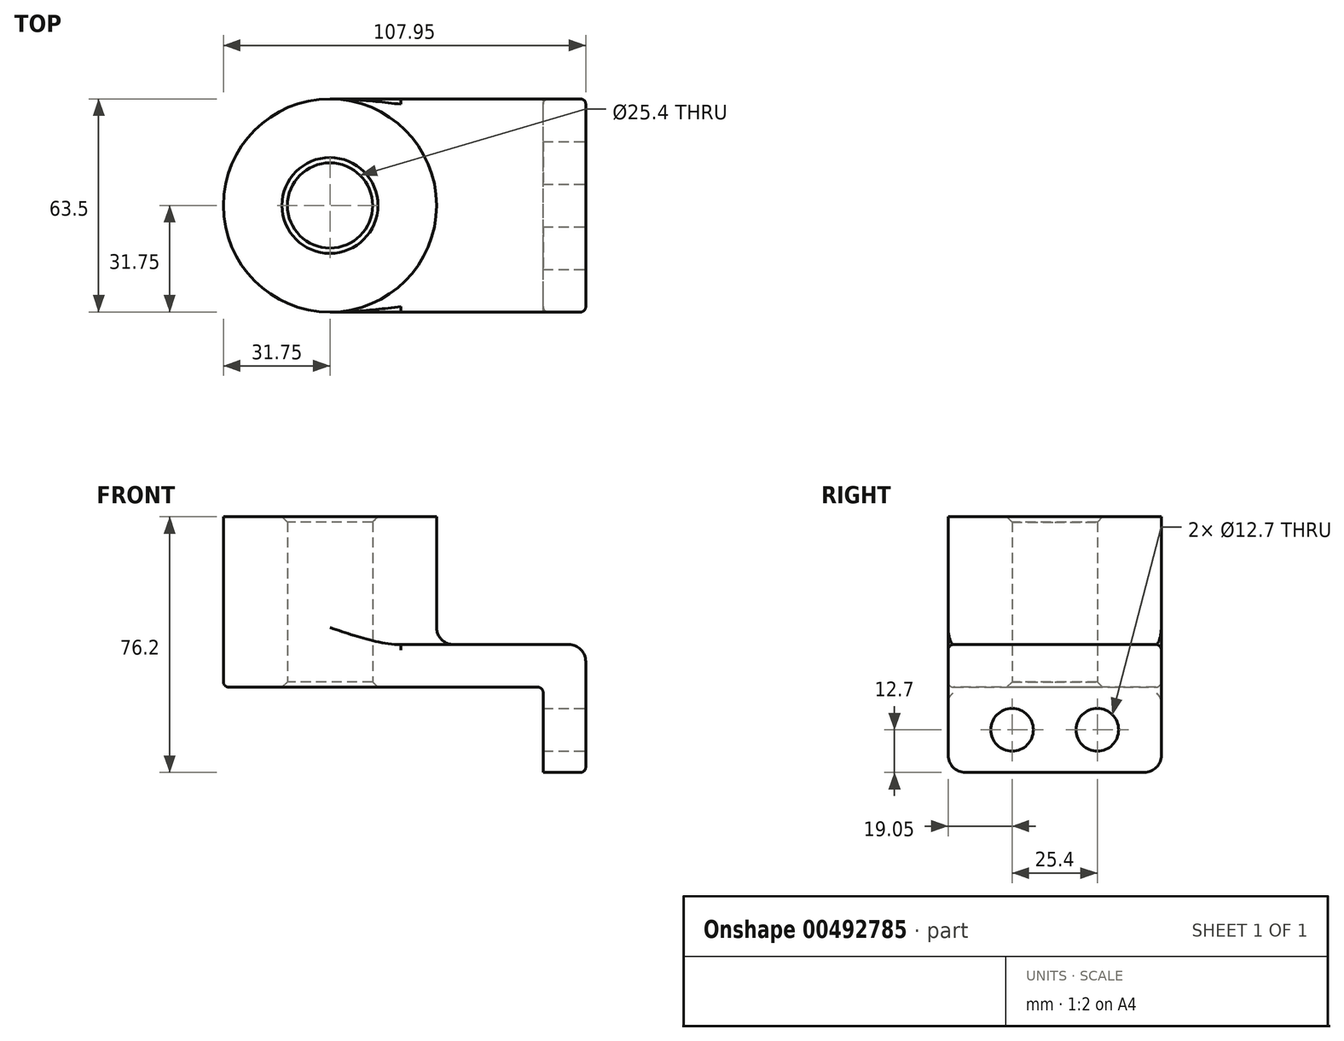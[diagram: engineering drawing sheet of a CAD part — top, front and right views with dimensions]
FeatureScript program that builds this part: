
annotation { "Feature Type Name" : "Feature", "Feature Type Description" : "" }
export const myFeature = defineFeature(function(context is Context, id is Id, definition is map)
    precondition{}
    {
        {
            var Q0;
            Q0=qCreatedBy(makeId("Top.planeOp"),FACE);
            var sketch = newSketch(context, id + "F0", { "sketchPlane" : qUnion([Q0])});
            skLineSegment(sketch, "E0.bottom", {"start": v(-38.1, -31.75) * mm, "end": v(38.1, -31.75) * mm});
            skLineSegment(sketch, "E0.top", {"start": v(-38.1, 31.75) * mm, "end": v(38.1, 31.75) * mm});
            skLineSegment(sketch, "E0.left", {"start": v(-38.1, -31.75) * mm, "end": v(-38.1, 31.75) * mm});
            skLineSegment(sketch, "E0.right", {"start": v(38.1, -31.75) * mm, "end": v(38.1, 31.75) * mm});
            skPoint(sketch, "E0.middle", {"position": v(0, 0) * mm});
            skCircle(sketch, "E1", {"center": v(-38.1, 0) * mm, "radius": 31.75 * mm});
            skCircle(sketch, "E2", {"center": v(-38.1, 0) * mm, "radius": 12.7 * mm});
            skSolve(sketch);
        }
        {
            var Q0;
            {var subQ0=sQuery(id+"F0.wireOp",EDGE,"E0.bottom");Q0=makeQuery(id+"F0.imprint","IMPRINT",FACE,{"disambiguationData":[TD([[makeQuery(id+"F0.imprint","IMPRINT",EDGE,{"derivedFrom":subQ0}),1.0]])]});}
            var Q1;
            {var subQ1=sQuery(id+"F0.wireOp",EDGE,"E0.left");var subQ3=sQuery(id+"F0.wireOp",EDGE,"E2");var subQ4=makeQuery(id+"F0.imprint","INTERSECT",VERTEX,{"disambiguationData":[OD(0.0)],"derivedFrom":[subQ1,subQ3]});Q1=makeQuery(id+"F0.imprint","IMPRINT",FACE,{"disambiguationData":[TD([[makeQuery(id+"F0.imprint","IMPRINT",EDGE,{"disambiguationData":[TD([[subQ4,-1.0]])],"derivedFrom":subQ3}),-1.0]])]});}
            var Q2;
            {var subQ1=sQuery(id+"F0.wireOp",EDGE,"E0.left");var subQ3=sQuery(id+"F0.wireOp",EDGE,"E2");var subQ4=makeQuery(id+"F0.imprint","INTERSECT",VERTEX,{"disambiguationData":[OD(0.0)],"derivedFrom":[subQ1,subQ3]});Q2=makeQuery(id+"F0.imprint","IMPRINT",FACE,{"disambiguationData":[TD([[makeQuery(id+"F0.imprint","IMPRINT",EDGE,{"disambiguationData":[TD([[subQ4,1.0]])],"derivedFrom":subQ3}),-1.0]])]});}
            extrude(context, id + "F1", {"entities" : qUnion([Q0, Q1, Q2]), "depth" : 12.7 * mm});
        }
        {
            var Q0;
            {var subQ1=sQuery(id+"F0.wireOp",EDGE,"E0.left");var subQ3=sQuery(id+"F0.wireOp",EDGE,"E2");var subQ4=makeQuery(id+"F0.imprint","INTERSECT",VERTEX,{"disambiguationData":[OD(0.0)],"derivedFrom":[subQ1,subQ3]});Q0=makeQuery(id+"F0.imprint","IMPRINT",FACE,{"disambiguationData":[TD([[makeQuery(id+"F0.imprint","IMPRINT",EDGE,{"disambiguationData":[TD([[subQ4,-1.0]])],"derivedFrom":subQ3}),-1.0]])]});}
            var Q1;
            {var subQ1=sQuery(id+"F0.wireOp",EDGE,"E0.left");var subQ3=sQuery(id+"F0.wireOp",EDGE,"E2");var subQ4=makeQuery(id+"F0.imprint","INTERSECT",VERTEX,{"disambiguationData":[OD(0.0)],"derivedFrom":[subQ1,subQ3]});Q1=makeQuery(id+"F0.imprint","IMPRINT",FACE,{"disambiguationData":[TD([[makeQuery(id+"F0.imprint","IMPRINT",EDGE,{"disambiguationData":[TD([[subQ4,1.0]])],"derivedFrom":subQ3}),-1.0]])]});}
            extrude(context, id + "F2", {"entities" : qUnion([Q0, Q1]), "operationType" : NewBodyOperationType.ADD, "depth" : 50.8 * mm});
        }
        {
            var Q0;
            Q0=makeQuery(id+"F1.opExtrude","SWEPT_FACE",FACE,{"disambiguationData":[OSD([sQuery(id+"F0.wireOp",EDGE,"E0.right")])]});
            var sketch = newSketch(context, id + "F3", { "sketchPlane" : qUnion([Q0])});
            skLineSegment(sketch, "E3.bottom", {"start": v(-31.75, 12.7) * mm, "end": v(31.75, 12.7) * mm});
            skLineSegment(sketch, "E3.top", {"start": v(-31.75, -25.4) * mm, "end": v(31.75, -25.4) * mm});
            skLineSegment(sketch, "E3.left", {"start": v(-31.75, 12.7) * mm, "end": v(-31.75, -25.4) * mm});
            skLineSegment(sketch, "E3.right", {"start": v(31.75, 12.7) * mm, "end": v(31.75, -25.4) * mm});
            skCircle(sketch, "E4", {"center": v(-12.7, -12.7) * mm, "radius": 6.35 * mm});
            skLineSegment(sketch, "E5", {"start": v(0, 0) * mm, "end": v(0, -25.4) * mm, "construction": true});
            skCircle(sketch, "E6.MirrorC", {"center": v(12.7, -12.7) * mm, "radius": 6.35 * mm});
            skSolve(sketch);
        }
        {
            var Q0;
            Q0 = qSketchRegion(id + "F3", true);
            extrude(context, id + "F4", {"entities" : qUnion([Q0]), "operationType" : NewBodyOperationType.ADD, "oppositeDirection" : true, "depth" : 12.7 * mm});
        }
        {
            var Q0;
            {var subQ0=sQuery(id+"F0.wireOp",EDGE,"E1");Q0=makeQuery(id+"F2.boolean.opBoolean","INTERSECT",EDGE,{"derivedFrom":[makeQuery(id+"F1.opExtrude","CAP_FACE",FACE,{"disambiguationData":[OSD([sQuery(id+"F0.wireOp",EDGE,"E0.bottom"),sQuery(id+"F0.wireOp",EDGE,"E0.top"),sQuery(id+"F0.wireOp",EDGE,"E0.right"),subQ0,sQuery(id+"F0.wireOp",EDGE,"E2")])],"isStart":false}),makeQuery(id+"F2.opExtrude","SWEPT_FACE",FACE,{"disambiguationData":[OSD([subQ0])]})]});}
            var Q1;
            Q1=makeQuery(id+"F4.opExtrude","SWEPT_EDGE",EDGE,{"disambiguationData":[OSD([sQuery(id+"F3.wireOp",EDGE,"E3.top"),sQuery(id+"F3.wireOp",EDGE,"E3.left")])]});
            var Q2;
            Q2=makeQuery(id+"F1.opExtrude","CAP_EDGE",EDGE,{"disambiguationData":[OSD([sQuery(id+"F0.wireOp",EDGE,"E0.right")])],"isStart":false});
            var Q3;
            Q3=makeQuery(id+"F4.opExtrude","SWEPT_EDGE",EDGE,{"disambiguationData":[OSD([sQuery(id+"F3.wireOp",EDGE,"E3.top"),sQuery(id+"F3.wireOp",EDGE,"E3.right")])]});
            fillet(context, id + "F5", {"entities" : qUnion([Q0, Q1, Q2, Q3]), "radius" : 5.08 * mm, "tangentPropagation" : true, "allowEdgeOverflow" : false});
        }
        {
            var Q0;
            Q0=makeQuery(id+"F1.opExtrude","CAP_EDGE",EDGE,{"disambiguationData":[OSD([sQuery(id+"F0.wireOp",EDGE,"E0.top")])],"isStart":false});
            var Q1;
            Q1=makeQuery(id+"F1.opExtrude","CAP_EDGE",EDGE,{"disambiguationData":[OSD([sQuery(id+"F0.wireOp",EDGE,"E0.top")])],"isStart":true});
            var Q2;
            Q2=makeQuery(id+"F4.boolean.opBoolean","INTERSECT",EDGE,{"derivedFrom":[makeQuery(id+"F1.opExtrude","CAP_FACE",FACE,{"disambiguationData":[OSD([sQuery(id+"F0.wireOp",EDGE,"E0.bottom"),sQuery(id+"F0.wireOp",EDGE,"E0.top"),sQuery(id+"F0.wireOp",EDGE,"E0.right"),sQuery(id+"F0.wireOp",EDGE,"E1"),sQuery(id+"F0.wireOp",EDGE,"E2")])],"isStart":true}),makeQuery(id+"F4.opExtrude","CAP_FACE",FACE,{"disambiguationData":[OSD([sQuery(id+"F3.wireOp",EDGE,"E3.bottom"),sQuery(id+"F3.wireOp",EDGE,"E3.top"),sQuery(id+"F3.wireOp",EDGE,"E3.left"),sQuery(id+"F3.wireOp",EDGE,"E3.right"),sQuery(id+"F3.wireOp",EDGE,"E4"),sQuery(id+"F3.wireOp",EDGE,"E6.MirrorC")])],"isStart":false})]});
            fillet(context, id + "F6", {"entities" : qUnion([Q0, Q1, Q2]), "radius" : 1.59 * mm, "tangentPropagation" : true, "allowEdgeOverflow" : false});
        }
        {
            var Q0;
            {var subQ0=sQuery(id+"F0.wireOp",EDGE,"E2");Q0=makeQuery(id+"F2.boolean.opBoolean","MERGE",FACE,{"derivedFrom":[makeQuery(id+"F1.opExtrude","SWEPT_FACE",FACE,{"disambiguationData":[OSD([subQ0])]}),makeQuery(id+"F2.opExtrude","SWEPT_FACE",FACE,{"disambiguationData":[OSD([subQ0])]})]});}
            chamfer(context, id + "F7", {"entities" : qUnion([Q0]), "width" : 1.59 * mm, "tangentPropagation" : true});
        }
    });
